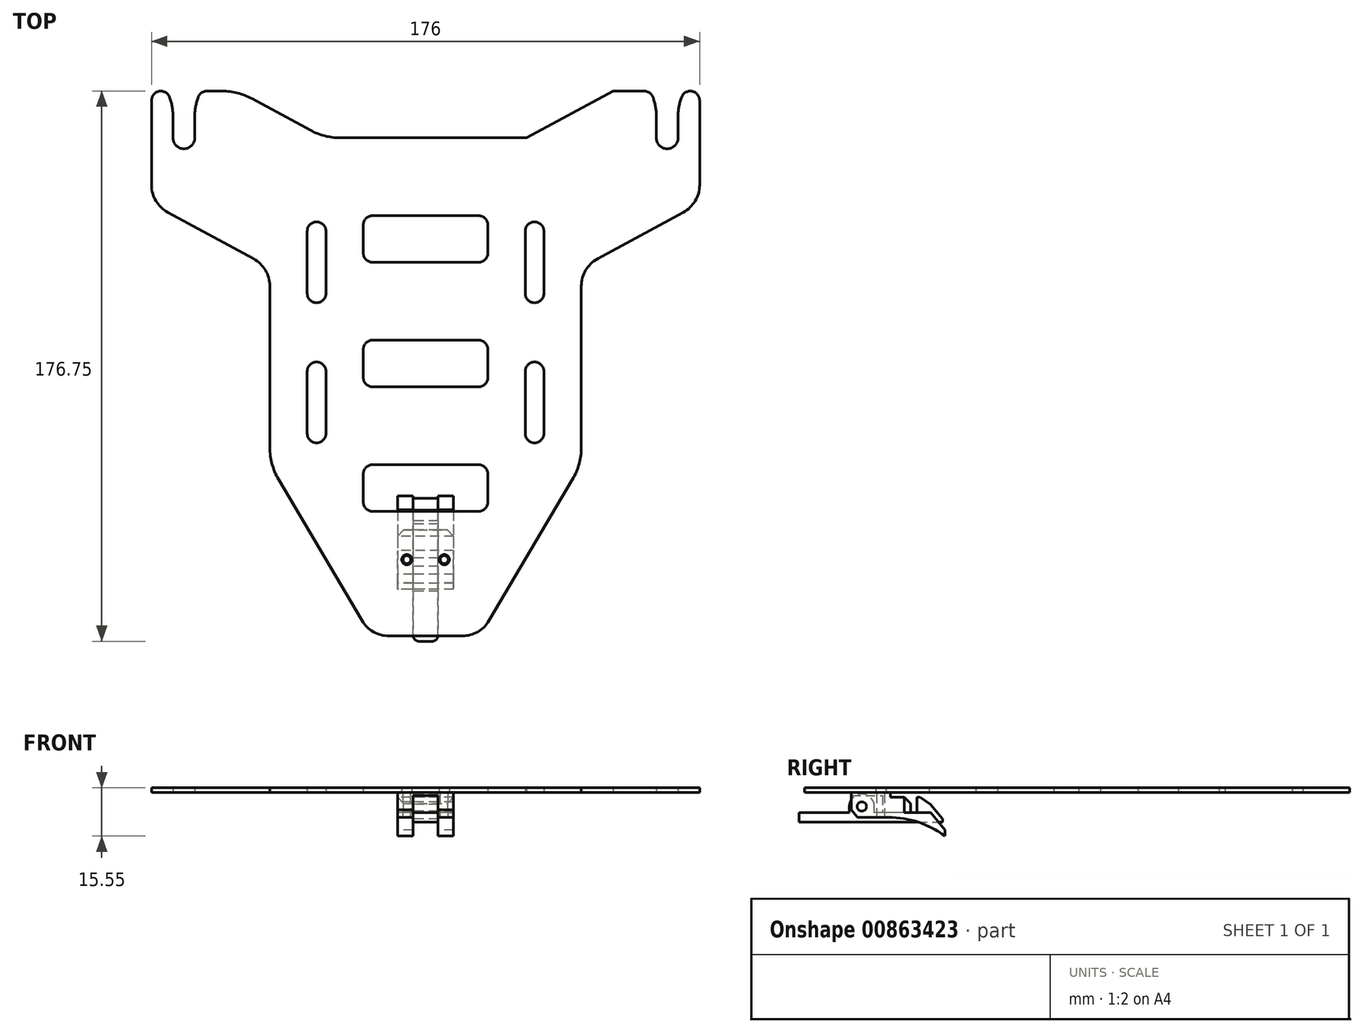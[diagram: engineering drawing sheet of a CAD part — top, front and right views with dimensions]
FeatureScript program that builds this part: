
annotation { "Feature Type Name" : "Feature", "Feature Type Description" : "" }
export const myFeature = defineFeature(function(context is Context, id is Id, definition is map)
    precondition{}
    {
        {
            var Q0;
            Q0=qCreatedBy(makeId("Top.planeOp"),FACE);
            var sketch = newSketch(context, id + "F0", { "sketchPlane" : qUnion([Q0])});
            skLineSegment(sketch, "E0", {"start": v(0, 0) * mm, "end": v(0, 155) * mm, "construction": true});
            skLineSegment(sketch, "E1", {"start": v(-74.1, 167) * mm, "end": v(-74.1, 160) * mm});
            skLineSegment(sketch, "E2", {"start": v(-74.1, 160) * mm, "end": v(-81.1, 160) * mm, "construction": true});
            skLineSegment(sketch, "E3", {"start": v(-88, 172) * mm, "end": v(-88, 144.84) * mm});
            skLineSegment(sketch, "E4", {"start": v(-82.76, 136.04) * mm, "end": v(-55.24, 121.14) * mm});
            skLineSegment(sketch, "E5", {"start": v(-50, 112.35) * mm, "end": v(-50, 60.47) * mm});
            skLineSegment(sketch, "E6", {"start": v(-47.22, 50.3) * mm, "end": v(-20.4, 4.91) * mm});
            skLineSegment(sketch, "E7", {"start": v(-11.8, 0) * mm, "end": v(0, 0) * mm});
            skArc(sketch, "E8", {"start": v(-82.19, 173.05) * mm, "mid": v(-85.53, 174.95) * mm, "end": v(-88, 172) * mm});
            skArc(sketch, "E9", {"start": v(-81.1, 160) * mm, "mid": v(-77.6, 156.5) * mm, "end": v(-74.1, 160) * mm});
            skPoint(sketch, "E10.visualSharp", {"position": v(-88, 138.88) * mm});
            skArc(sketch, "E10.filletArc", {"start": v(-88, 144.84) * mm, "mid": v(-86.6, 139.72) * mm, "end": v(-82.76, 136.04) * mm});
            skPoint(sketch, "E11.visualSharp", {"position": v(-50, 118.3) * mm});
            skArc(sketch, "E11.filletArc", {"start": v(-50, 112.35) * mm, "mid": v(-51.4, 117.46) * mm, "end": v(-55.24, 121.14) * mm});
            skPoint(sketch, "E12.visualSharp", {"position": v(-50, 55) * mm});
            skArc(sketch, "E12.filletArc", {"start": v(-50, 60.47) * mm, "mid": v(-49.3, 55.2) * mm, "end": v(-47.22, 50.3) * mm});
            skPoint(sketch, "E13.visualSharp", {"position": v(-17.5, 0) * mm});
            skArc(sketch, "E13.filletArc", {"start": v(-20.4, 4.91) * mm, "mid": v(-16.75, 1.31) * mm, "end": v(-11.8, 0) * mm});
            skLineSegment(sketch, "E14", {"start": v(-35, 130) * mm, "end": v(-35, 110) * mm, "construction": true});
            skLineSegment(sketch, "E15", {"start": v(-35, 110) * mm, "end": v(-35, 85) * mm, "construction": true});
            skLineSegment(sketch, "E16", {"start": v(-35, 85) * mm, "end": v(-35, 65) * mm, "construction": true});
            skLineSegment(sketch, "E17.bottom", {"start": v(-17, 135) * mm, "end": v(17, 135) * mm});
            skLineSegment(sketch, "E17.top", {"start": v(-17, 120) * mm, "end": v(17, 120) * mm});
            skLineSegment(sketch, "E17.left", {"start": v(-20, 132) * mm, "end": v(-20, 123) * mm});
            skLineSegment(sketch, "E17.right", {"start": v(20, 132) * mm, "end": v(20, 123) * mm});
            skPoint(sketch, "E17.middle", {"position": v(0, 127.5) * mm});
            skPoint(sketch, "E18.visualSharp", {"position": v(-20, 135) * mm});
            skArc(sketch, "E18.filletArc", {"start": v(-17, 135) * mm, "mid": v(-19.12, 134.12) * mm, "end": v(-20, 132) * mm});
            skPoint(sketch, "E19.visualSharp", {"position": v(-20, 120) * mm});
            skArc(sketch, "E19.filletArc", {"start": v(-20, 123) * mm, "mid": v(-19.12, 120.88) * mm, "end": v(-17, 120) * mm});
            skPoint(sketch, "E20.visualSharp", {"position": v(20, 120) * mm});
            skArc(sketch, "E20.filletArc", {"start": v(17, 120) * mm, "mid": v(19.12, 120.88) * mm, "end": v(20, 123) * mm});
            skPoint(sketch, "E21.visualSharp", {"position": v(20, 135) * mm});
            skArc(sketch, "E21.filletArc", {"start": v(20, 132) * mm, "mid": v(19.12, 134.12) * mm, "end": v(17, 135) * mm});
            skArc(sketch, "E22.0.startCap", {"start": v(-38, 130) * mm, "mid": v(-35, 133) * mm, "end": v(-32, 130) * mm});
            skArc(sketch, "E22.0.endCap", {"start": v(-32, 110) * mm, "mid": v(-35, 107) * mm, "end": v(-38, 110) * mm});
            skLineSegment(sketch, "E22.0.left", {"start": v(-32, 130) * mm, "end": v(-32, 110) * mm});
            skLineSegment(sketch, "E22.0.right", {"start": v(-38, 130) * mm, "end": v(-38, 110) * mm});
            skArc(sketch, "E23.0.startCap", {"start": v(-38, 85) * mm, "mid": v(-35, 88) * mm, "end": v(-32, 85) * mm});
            skArc(sketch, "E23.0.endCap", {"start": v(-32, 65) * mm, "mid": v(-35, 62) * mm, "end": v(-38, 65) * mm});
            skLineSegment(sketch, "E23.0.left", {"start": v(-32, 85) * mm, "end": v(-32, 65) * mm});
            skLineSegment(sketch, "E23.0.right", {"start": v(-38, 85) * mm, "end": v(-38, 65) * mm});
            skPoint(sketch, "E24.MirrorP", {"position": v(17.5, 0) * mm});
            skPoint(sketch, "E25.0.1.0", {"position": v(20, 80) * mm});
            skLineSegment(sketch, "E25.0.1.1", {"start": v(-17, 80) * mm, "end": v(17, 80) * mm});
            skPoint(sketch, "E25.0.1.2", {"position": v(20, 95) * mm});
            skPoint(sketch, "E25.0.1.3", {"position": v(-20, 80) * mm});
            skLineSegment(sketch, "E25.0.1.4", {"start": v(-17, 95) * mm, "end": v(17, 95) * mm});
            skArc(sketch, "E25.0.1.5", {"start": v(20, 92) * mm, "mid": v(19.12, 94.12) * mm, "end": v(17, 95) * mm});
            skArc(sketch, "E25.0.1.6", {"start": v(17, 80) * mm, "mid": v(19.12, 80.88) * mm, "end": v(20, 83) * mm});
            skArc(sketch, "E25.0.1.7", {"start": v(-20, 83) * mm, "mid": v(-19.12, 80.88) * mm, "end": v(-17, 80) * mm});
            skLineSegment(sketch, "E25.0.1.8", {"start": v(-20, 92) * mm, "end": v(-20, 83) * mm});
            skLineSegment(sketch, "E25.0.1.9", {"start": v(20, 92) * mm, "end": v(20, 83) * mm});
            skPoint(sketch, "E25.0.1.10", {"position": v(0, 87.5) * mm});
            skArc(sketch, "E25.0.1.11", {"start": v(-17, 95) * mm, "mid": v(-19.12, 94.12) * mm, "end": v(-20, 92) * mm});
            skPoint(sketch, "E25.0.1.12", {"position": v(-20, 95) * mm});
            skPoint(sketch, "E25.0.1.13", {"position": v(0, 87.5) * mm});
            skPoint(sketch, "E25.0.2.0", {"position": v(20, 40) * mm});
            skLineSegment(sketch, "E25.0.2.1", {"start": v(-17, 40) * mm, "end": v(17, 40) * mm});
            skPoint(sketch, "E25.0.2.2", {"position": v(20, 55) * mm});
            skPoint(sketch, "E25.0.2.3", {"position": v(-20, 40) * mm});
            skLineSegment(sketch, "E25.0.2.4", {"start": v(-17, 55) * mm, "end": v(17, 55) * mm});
            skArc(sketch, "E25.0.2.5", {"start": v(20, 52) * mm, "mid": v(19.12, 54.12) * mm, "end": v(17, 55) * mm});
            skArc(sketch, "E25.0.2.6", {"start": v(17, 40) * mm, "mid": v(19.12, 40.88) * mm, "end": v(20, 43) * mm});
            skArc(sketch, "E25.0.2.7", {"start": v(-20, 43) * mm, "mid": v(-19.12, 40.88) * mm, "end": v(-17, 40) * mm});
            skLineSegment(sketch, "E25.0.2.8", {"start": v(-20, 52) * mm, "end": v(-20, 43) * mm});
            skLineSegment(sketch, "E25.0.2.9", {"start": v(20, 52) * mm, "end": v(20, 43) * mm});
            skPoint(sketch, "E25.0.2.10", {"position": v(0, 47.5) * mm});
            skArc(sketch, "E25.0.2.11", {"start": v(-17, 55) * mm, "mid": v(-19.12, 54.12) * mm, "end": v(-20, 52) * mm});
            skPoint(sketch, "E25.0.2.12", {"position": v(-20, 55) * mm});
            skPoint(sketch, "E25.0.2.13", {"position": v(0, 47.5) * mm});
            skLineSegment(sketch, "E25.direction1", {"start": v(-26.51, 120) * mm, "end": v(-20, 120) * mm, "construction": true});
            skLineSegment(sketch, "E25.direction2", {"start": v(-20, 120) * mm, "end": v(-20, 80) * mm, "construction": true});
            skLineSegment(sketch, "E26", {"start": v(-6, 24.5) * mm, "end": v(6, 24.5) * mm, "construction": true});
            skLineSegment(sketch, "E27", {"start": v(-81.1, 160) * mm, "end": v(-81.1, 167) * mm});
            skArc(sketch, "E28", {"start": v(-81.1, 167) * mm, "mid": v(-81.37, 170.07) * mm, "end": v(-82.19, 173.05) * mm});
            skArc(sketch, "E29", {"start": v(-73.01, 173.05) * mm, "mid": v(-73.83, 170.07) * mm, "end": v(-74.1, 167) * mm});
            skArc(sketch, "E30", {"start": v(-70.2, 175) * mm, "mid": v(-71.91, 174.46) * mm, "end": v(-73.01, 173.05) * mm});
            skLineSegment(sketch, "E31", {"start": v(-70.2, 175) * mm, "end": v(-65.27, 175) * mm});
            skLineSegment(sketch, "E32", {"start": v(-36.96, 162.41) * mm, "end": v(-55.74, 172.59) * mm});
            skLineSegment(sketch, "E33", {"start": v(-27.43, 160) * mm, "end": v(0, 160) * mm});
            skLineSegment(sketch, "E34.MirrorCS", {"start": v(32.5, 160) * mm, "end": v(0, 160) * mm});
            skLineSegment(sketch, "E35.MirrorCS", {"start": v(47.22, 50.3) * mm, "end": v(20.4, 4.91) * mm});
            skArc(sketch, "E36.MirrorCS", {"start": v(20.4, 4.91) * mm, "mid": v(16.75, 1.31) * mm, "end": v(11.8, 0) * mm});
            skLineSegment(sketch, "E37.MirrorCS", {"start": v(11.8, 0) * mm, "end": v(0, 0) * mm});
            skArc(sketch, "E38.MirrorCS", {"start": v(70.2, 175) * mm, "mid": v(71.91, 174.46) * mm, "end": v(73.01, 173.05) * mm});
            skArc(sketch, "E39.MirrorCS", {"start": v(81.1, 167) * mm, "mid": v(81.37, 170.07) * mm, "end": v(82.19, 173.05) * mm});
            skArc(sketch, "E40.MirrorCS", {"start": v(50, 112.35) * mm, "mid": v(51.4, 117.46) * mm, "end": v(55.24, 121.14) * mm});
            skArc(sketch, "E41.MirrorCS", {"start": v(32, 65) * mm, "mid": v(35, 62) * mm, "end": v(38, 65) * mm});
            skArc(sketch, "E42.MirrorCS", {"start": v(88, 144.84) * mm, "mid": v(86.6, 139.72) * mm, "end": v(82.76, 136.04) * mm});
            skLineSegment(sketch, "E43.MirrorCS", {"start": v(74.1, 160) * mm, "end": v(81.1, 160) * mm, "construction": true});
            skLineSegment(sketch, "E44.MirrorCS", {"start": v(81.1, 160) * mm, "end": v(81.1, 167) * mm});
            skArc(sketch, "E45.MirrorCS", {"start": v(50, 60.47) * mm, "mid": v(49.3, 55.2) * mm, "end": v(47.22, 50.3) * mm});
            skLineSegment(sketch, "E46.MirrorCS", {"start": v(82.76, 136.04) * mm, "end": v(55.24, 121.14) * mm});
            skLineSegment(sketch, "E47.MirrorCS", {"start": v(88, 172) * mm, "end": v(88, 144.84) * mm});
            skLineSegment(sketch, "E48.MirrorCS", {"start": v(35, 110) * mm, "end": v(35, 85) * mm, "construction": true});
            skArc(sketch, "E49.MirrorCS", {"start": v(73.01, 173.05) * mm, "mid": v(73.83, 170.07) * mm, "end": v(74.1, 167) * mm});
            skLineSegment(sketch, "E50.MirrorCS", {"start": v(70.2, 175) * mm, "end": v(60.2, 175) * mm});
            skLineSegment(sketch, "E51.MirrorCS", {"start": v(35, 85) * mm, "end": v(35, 65) * mm, "construction": true});
            skLineSegment(sketch, "E52.MirrorCS", {"start": v(35, 130) * mm, "end": v(35, 110) * mm, "construction": true});
            skLineSegment(sketch, "E53.MirrorCS", {"start": v(32.5, 160) * mm, "end": v(60.2, 175) * mm});
            skLineSegment(sketch, "E54.MirrorCS", {"start": v(38, 130) * mm, "end": v(38, 110) * mm});
            skPoint(sketch, "E55.MirrorP", {"position": v(50, 118.3) * mm});
            skPoint(sketch, "E56.MirrorP", {"position": v(88, 138.88) * mm});
            skLineSegment(sketch, "E57.MirrorCS", {"start": v(50, 112.35) * mm, "end": v(50, 60.47) * mm});
            skLineSegment(sketch, "E58.MirrorCS", {"start": v(74.1, 167) * mm, "end": v(74.1, 160) * mm});
            skLineSegment(sketch, "E59.MirrorCS", {"start": v(32, 85) * mm, "end": v(32, 65) * mm});
            skPoint(sketch, "E60.MirrorP", {"position": v(50, 55) * mm});
            skArc(sketch, "E61.MirrorCS", {"start": v(82.19, 173.05) * mm, "mid": v(85.53, 174.95) * mm, "end": v(88, 172) * mm});
            skArc(sketch, "E62.MirrorCS", {"start": v(32, 110) * mm, "mid": v(35, 107) * mm, "end": v(38, 110) * mm});
            skLineSegment(sketch, "E63.MirrorCS", {"start": v(38, 85) * mm, "end": v(38, 65) * mm});
            skLineSegment(sketch, "E64.MirrorCS", {"start": v(32, 130) * mm, "end": v(32, 110) * mm});
            skArc(sketch, "E65.MirrorCS", {"start": v(38, 130) * mm, "mid": v(35, 133) * mm, "end": v(32, 130) * mm});
            skArc(sketch, "E66.MirrorCS", {"start": v(38, 85) * mm, "mid": v(35, 88) * mm, "end": v(32, 85) * mm});
            skArc(sketch, "E67.MirrorCS", {"start": v(81.1, 160) * mm, "mid": v(77.6, 156.5) * mm, "end": v(74.1, 160) * mm});
            skPoint(sketch, "E68.visualSharp", {"position": v(-32.5, 160) * mm});
            skArc(sketch, "E68.filletArc", {"start": v(-36.96, 162.41) * mm, "mid": v(-32.34, 160.61) * mm, "end": v(-27.43, 160) * mm});
            skPoint(sketch, "E69.visualSharp", {"position": v(-60.2, 175) * mm});
            skArc(sketch, "E69.filletArc", {"start": v(-55.74, 172.59) * mm, "mid": v(-60.36, 174.39) * mm, "end": v(-65.27, 175) * mm});
            skSolve(sketch);
        }
        {
            var Q0;
            Q0=makeQuery(id+"F0.imprint","IMPRINT",FACE,{"disambiguationData":[TD([[makeQuery(id+"F0.imprint","IMPRINT",EDGE,{"derivedFrom":sQuery(id+"F0.wireOp",EDGE,"E1")}),1.0]])]});
            extrude(context, id + "F1", {"entities" : qUnion([Q0]), "offsetDistance" : 25 * mm, "depth" : 1.55 * mm});
        }
        {
            var Q0;
            Q0=sQuery(id+"F0.wireOp",VERTEX,"E26.start");
            var Q1;
            Q1=sQuery(id+"F0.wireOp",VERTEX,"E26.end");
            var Q2;
            Q2=makeQuery(id+"F1.opExtrude","SWEPT_BODY",BODY,{"disambiguationData":[OSD([sQuery(id+"F0.wireOp",EDGE,"40a4Gtip-nmCk-8SGa-D8cc-ILroSEPhkYNr"),sQuery(id+"F0.wireOp",EDGE,"E1"),sQuery(id+"F0.wireOp",EDGE,"AO4oYKKv-FQzy-DXXs-Zy1O-bGXR8dVoVOAc"),sQuery(id+"F0.wireOp",EDGE,"E3"),sQuery(id+"F0.wireOp",EDGE,"E4"),sQuery(id+"F0.wireOp",EDGE,"E5"),sQuery(id+"F0.wireOp",EDGE,"E6"),sQuery(id+"F0.wireOp",EDGE,"E7"),sQuery(id+"F0.wireOp",EDGE,"E8"),sQuery(id+"F0.wireOp",EDGE,"E9"),sQuery(id+"F0.wireOp",EDGE,"0da25941-dc92-4c08-8014-236c1829b156.filletArc"),sQuery(id+"F0.wireOp",EDGE,"E10.filletArc"),sQuery(id+"F0.wireOp",EDGE,"E11.filletArc"),sQuery(id+"F0.wireOp",EDGE,"E12.filletArc"),sQuery(id+"F0.wireOp",EDGE,"E13.filletArc"),sQuery(id+"F0.wireOp",EDGE,"E17.bottom"),sQuery(id+"F0.wireOp",EDGE,"E17.top"),sQuery(id+"F0.wireOp",EDGE,"E17.left"),sQuery(id+"F0.wireOp",EDGE,"E17.right"),sQuery(id+"F0.wireOp",EDGE,"E18.filletArc"),sQuery(id+"F0.wireOp",EDGE,"E19.filletArc"),sQuery(id+"F0.wireOp",EDGE,"E20.filletArc"),sQuery(id+"F0.wireOp",EDGE,"E21.filletArc"),sQuery(id+"F0.wireOp",EDGE,"E22.0.startCap"),sQuery(id+"F0.wireOp",EDGE,"E22.0.endCap"),sQuery(id+"F0.wireOp",EDGE,"E22.0.left"),sQuery(id+"F0.wireOp",EDGE,"E22.0.right"),sQuery(id+"F0.wireOp",EDGE,"E23.0.startCap"),sQuery(id+"F0.wireOp",EDGE,"E23.0.endCap"),sQuery(id+"F0.wireOp",EDGE,"E23.0.left"),sQuery(id+"F0.wireOp",EDGE,"E23.0.right"),sQuery(id+"F0.wireOp",EDGE,"c865a5f4-4d62-4504-be47-4ccb92e482130.MirrorCS"),sQuery(id+"F0.wireOp",EDGE,"c865a5f4-4d62-4504-be47-4ccb92e482131.MirrorCS"),sQuery(id+"F0.wireOp",EDGE,"c865a5f4-4d62-4504-be47-4ccb92e482132.MirrorCS"),sQuery(id+"F0.wireOp",EDGE,"c865a5f4-4d62-4504-be47-4ccb92e482133.MirrorCS"),sQuery(id+"F0.wireOp",EDGE,"c865a5f4-4d62-4504-be47-4ccb92e482135.MirrorCS"),sQuery(id+"F0.wireOp",EDGE,"c865a5f4-4d62-4504-be47-4ccb92e482137.MirrorCS"),sQuery(id+"F0.wireOp",EDGE,"c865a5f4-4d62-4504-be47-4ccb92e482138.MirrorCS"),sQuery(id+"F0.wireOp",EDGE,"c865a5f4-4d62-4504-be47-4ccb92e4821310.MirrorCS"),sQuery(id+"F0.wireOp",EDGE,"c865a5f4-4d62-4504-be47-4ccb92e4821311.MirrorCS"),sQuery(id+"F0.wireOp",EDGE,"c865a5f4-4d62-4504-be47-4ccb92e4821312.MirrorCS"),sQuery(id+"F0.wireOp",EDGE,"c865a5f4-4d62-4504-be47-4ccb92e4821314.MirrorCS"),sQuery(id+"F0.wireOp",EDGE,"c865a5f4-4d62-4504-be47-4ccb92e4821316.MirrorCS"),sQuery(id+"F0.wireOp",EDGE,"c865a5f4-4d62-4504-be47-4ccb92e4821317.MirrorCS"),sQuery(id+"F0.wireOp",EDGE,"c865a5f4-4d62-4504-be47-4ccb92e4821318.MirrorCS"),sQuery(id+"F0.wireOp",EDGE,"c865a5f4-4d62-4504-be47-4ccb92e4821320.MirrorCS"),sQuery(id+"F0.wireOp",EDGE,"c865a5f4-4d62-4504-be47-4ccb92e4821322.MirrorCS"),sQuery(id+"F0.wireOp",EDGE,"c865a5f4-4d62-4504-be47-4ccb92e4821323.MirrorCS"),sQuery(id+"F0.wireOp",EDGE,"c865a5f4-4d62-4504-be47-4ccb92e4821324.MirrorCS"),sQuery(id+"F0.wireOp",EDGE,"c865a5f4-4d62-4504-be47-4ccb92e4821325.MirrorCS"),sQuery(id+"F0.wireOp",EDGE,"c865a5f4-4d62-4504-be47-4ccb92e4821326.MirrorCS"),sQuery(id+"F0.wireOp",EDGE,"c865a5f4-4d62-4504-be47-4ccb92e4821328.MirrorCS"),sQuery(id+"F0.wireOp",EDGE,"c865a5f4-4d62-4504-be47-4ccb92e4821329.MirrorCS"),sQuery(id+"F0.wireOp",EDGE,"c865a5f4-4d62-4504-be47-4ccb92e4821330.MirrorCS"),sQuery(id+"F0.wireOp",EDGE,"E25.0.1.1"),sQuery(id+"F0.wireOp",EDGE,"E25.0.1.4"),sQuery(id+"F0.wireOp",EDGE,"E25.0.1.5"),sQuery(id+"F0.wireOp",EDGE,"E25.0.1.6"),sQuery(id+"F0.wireOp",EDGE,"E25.0.1.7"),sQuery(id+"F0.wireOp",EDGE,"E25.0.1.8"),sQuery(id+"F0.wireOp",EDGE,"E25.0.1.9"),sQuery(id+"F0.wireOp",EDGE,"E25.0.1.11"),sQuery(id+"F0.wireOp",EDGE,"E25.0.2.1"),sQuery(id+"F0.wireOp",EDGE,"E25.0.2.4"),sQuery(id+"F0.wireOp",EDGE,"E25.0.2.5"),sQuery(id+"F0.wireOp",EDGE,"E25.0.2.6"),sQuery(id+"F0.wireOp",EDGE,"E25.0.2.7"),sQuery(id+"F0.wireOp",EDGE,"E25.0.2.8"),sQuery(id+"F0.wireOp",EDGE,"E25.0.2.9"),sQuery(id+"F0.wireOp",EDGE,"E25.0.2.11")])]});
            hole(context, id + "F2", {"style" : HoleStyle.SIMPLE, "endStyle" : HoleEndStyle.THROUGH, "oppositeDirection" : true, "standardTappedOrClearance" : lookupTablePath({ "standard" : "ISO", "fit" : "Normal", "size" : "M3", "type" : "Clearance" }), "standardBlindInLast" : lookupTablePath({ "fit" : "Standard", "standard" : "ISO", "size" : "M3", "type" : "Clearance" }), "holeDiameter" : 3.3 * mm, "isTappedThrough" : true, "tappedDepth" : 3.5 * mm, "tapClearance" : 3, "locations" : qUnion([Q0, Q1]), "scope" : qUnion([Q2])});
        }
        {
            var Q0;
            Q0=qCreatedBy(makeId("Right.planeOp"),FACE);
            var sketch = newSketch(context, id + "F3", { "sketchPlane" : qUnion([Q0])});
            skLineSegment(sketch, "E70", {"start": v(15, 0) * mm, "end": v(15, -5.62) * mm});
            skLineSegment(sketch, "E71", {"start": v(15, -5.62) * mm, "end": v(17, -8) * mm});
            skLineSegment(sketch, "E72", {"start": v(17, -8) * mm, "end": v(27, -8) * mm});
            skArc(sketch, "E73", {"start": v(45, -14) * mm, "mid": v(36.49, -9.54) * mm, "end": v(27, -8) * mm});
            skLineSegment(sketch, "E74", {"start": v(45, -14) * mm, "end": v(45, -12) * mm});
            skLineSegment(sketch, "E75", {"start": v(45, -12) * mm, "end": v(40.5, -6.5) * mm});
            skLineSegment(sketch, "E76", {"start": v(40.5, -6.5) * mm, "end": v(34, -6.5) * mm});
            skLineSegment(sketch, "E77", {"start": v(34, -6.5) * mm, "end": v(34, -1.5) * mm});
            skLineSegment(sketch, "E78", {"start": v(34, -1.5) * mm, "end": v(27.5, -1.5) * mm});
            skLineSegment(sketch, "E79", {"start": v(27.5, -1.5) * mm, "end": v(27.5, 0) * mm});
            skLineSegment(sketch, "E80", {"start": v(27.5, 0) * mm, "end": v(15, 0) * mm});
            skCircle(sketch, "E81", {"center": v(18.35, -4.5) * mm, "radius": 1.5 * mm});
            skLineSegment(sketch, "E82", {"start": v(15, -1) * mm, "end": v(25, -1) * mm});
            skLineSegment(sketch, "E83", {"start": v(25, -1) * mm, "end": v(25, -8) * mm});
            skLineSegment(sketch, "E84", {"start": v(34, -6.5) * mm, "end": v(25, -6.5) * mm});
            skSolve(sketch);
        }
        {
            var Q0;
            Q0=qSketchRegion(id+"F3",true);
            extrude(context, id + "F4", {"entities" : qUnion([Q0]), "endBound" : BoundingType.SYMMETRIC, "depth" : 18 * mm});
        }
        {
            var Q0;
            {var subQ0=sQuery(id+"F3.wireOp",EDGE,"E71");Q0=makeQuery(id+"F3.imprint","IMPRINT",FACE,{"disambiguationData":[TD([[makeQuery(id+"F3.imprint","IMPRINT",EDGE,{"derivedFrom":subQ0}),1.0]])]});}
            var Q1;
            {var subQ1=sQuery(id+"F3.wireOp",EDGE,"E73");Q1=makeQuery(id+"F3.imprint","IMPRINT",FACE,{"disambiguationData":[TD([[makeQuery(id+"F3.imprint","IMPRINT",EDGE,{"derivedFrom":subQ1}),-1.0]])]});}
            extrude(context, id + "F5", {"entities" : qUnion([Q0, Q1]), "operationType" : NewBodyOperationType.REMOVE, "endBound" : BoundingType.SYMMETRIC, "depth" : 8 * mm});
        }
        {
            var Q0;
            Q0=qCreatedBy(makeId("Right.planeOp"),FACE);
            var sketch = newSketch(context, id + "F6", { "sketchPlane" : qUnion([Q0])});
            skLineSegment(sketch, "E85", {"start": v(-1.75, -9.5) * mm, "end": v(44.25, -9.5) * mm});
            skLineSegment(sketch, "E86", {"start": v(44.25, -9.5) * mm, "end": v(44.25, -8.5) * mm});
            skLineSegment(sketch, "E87", {"start": v(37, -1.5) * mm, "end": v(36, -1.5) * mm});
            skLineSegment(sketch, "E88", {"start": v(36, -1.5) * mm, "end": v(36, -6.5) * mm});
            skLineSegment(sketch, "E89", {"start": v(36, -6.5) * mm, "end": v(22.35, -6.5) * mm});
            skLineSegment(sketch, "E90", {"start": v(22.35, -6.5) * mm, "end": v(22.35, -4.5) * mm});
            skLineSegment(sketch, "E91", {"start": v(14.35, -4.5) * mm, "end": v(14.35, -6.5) * mm});
            skLineSegment(sketch, "E92", {"start": v(14.35, -6.5) * mm, "end": v(-1.75, -6.5) * mm});
            skLineSegment(sketch, "E93", {"start": v(-1.75, -6.5) * mm, "end": v(-1.75, -9.5) * mm});
            skArc(sketch, "E94", {"start": v(22.35, -4.5) * mm, "mid": v(18.35, -0.5) * mm, "end": v(14.35, -4.5) * mm});
            skLineSegment(sketch, "E95", {"start": v(44.25, -8.5) * mm, "end": v(40.34, -3.84) * mm});
            skLineSegment(sketch, "E96", {"start": v(40.34, -3.84) * mm, "end": v(37, -1.5) * mm});
            skCircle(sketch, "E97.0", {"center": v(18.35, -4.5) * mm, "radius": 1.5 * mm});
            skSolve(sketch);
        }
        {
            var Q0;
            Q0=qSketchRegion(id+"F6",true);
            extrude(context, id + "F7", {"entities" : qUnion([Q0]), "endBound" : BoundingType.SYMMETRIC, "depth" : 8 * mm});
        }
        {
            var Q0;
            Q0=sQuery(id+"F0.wireOp",VERTEX,"E26.end");
            var Q1;
            Q1=sQuery(id+"F0.wireOp",VERTEX,"E26.start");
            var Q2;
            Q2=makeQuery(id+"F4.opExtrude","SWEPT_BODY",BODY,{"disambiguationData":[OSD([sQuery(id+"F3.wireOp",EDGE,"E70"),sQuery(id+"F3.wireOp",EDGE,"E71"),sQuery(id+"F3.wireOp",EDGE,"E72"),sQuery(id+"F3.wireOp",EDGE,"E73"),sQuery(id+"F3.wireOp",EDGE,"E74"),sQuery(id+"F3.wireOp",EDGE,"E75"),sQuery(id+"F3.wireOp",EDGE,"E76"),sQuery(id+"F3.wireOp",EDGE,"E77"),sQuery(id+"F3.wireOp",EDGE,"E78"),sQuery(id+"F3.wireOp",EDGE,"E79"),sQuery(id+"F3.wireOp",EDGE,"E80"),sQuery(id+"F3.wireOp",EDGE,"E81")])]});
            hole(context, id + "F8", {"style" : HoleStyle.SIMPLE, "endStyle" : HoleEndStyle.THROUGH, "standardTappedOrClearance" : lookupTablePath({ "standard" : "ISO", "engagement" : "75%", "pitch" : "0.5 mm", "size" : "M3", "type" : "Tapped" }), "standardBlindInLast" : lookupTablePath({ "standard" : "ISO", "engagement" : "75%", "pitch" : "0.5 mm", "size" : "M3", "type" : "Tapped" }), "holeDiameter" : 2.5 * mm, "showTappedDepth" : true, "isTappedThrough" : true, "tappedDepth" : 3.5 * mm, "tapClearance" : 3, "locations" : qUnion([Q0, Q1]), "scope" : qUnion([Q2]), "majorDiameter" : 3 * mm});
        }
        {
            var Q0;
            Q0=makeQuery(id+"F4.opExtrude","CAP_EDGE",EDGE,{"disambiguationData":[OSD([sQuery(id+"F3.wireOp",EDGE,"E77")])],"isStart":false});
            var Q1;
            Q1=makeQuery(id+"F4.opExtrude","CAP_EDGE",EDGE,{"disambiguationData":[OSD([sQuery(id+"F3.wireOp",EDGE,"E77")])],"isStart":true});
            var Q2;
            Q2=makeQuery(id+"F4.opExtrude","SWEPT_EDGE",EDGE,{"disambiguationData":[OSD([sQuery(id+"F3.wireOp",EDGE,"E77"),sQuery(id+"F3.wireOp",EDGE,"E78")])]});
            chamfer(context, id + "F9", {"entities" : qUnion([Q0, Q1, Q2]), "width" : 2 * mm, "tangentPropagation" : true});
        }
        {
            var Q0;
            Q0=makeQuery(id+"F7.opExtrude","CAP_EDGE",EDGE,{"disambiguationData":[OSD([sQuery(id+"F6.wireOp",EDGE,"E93")])],"isStart":true});
            var Q1;
            Q1=makeQuery(id+"F7.opExtrude","CAP_EDGE",EDGE,{"disambiguationData":[OSD([sQuery(id+"F6.wireOp",EDGE,"E93")])],"isStart":false});
            fillet(context, id + "F10", {"entities" : qUnion([Q0, Q1]), "radius" : 2 * mm, "tangentPropagation" : true, "allowEdgeOverflow" : false});
        }
    });
